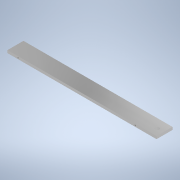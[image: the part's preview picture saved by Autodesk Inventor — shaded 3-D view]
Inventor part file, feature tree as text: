
AUTODESK INVENTOR PART (.ipt)
format: ipt  version: 2022 (Build 260153000, 153)  size: 131,584 bytes
history: native  units: mm
features: sketch x3, hole x2, other x1, extrude x1
ambient origin geometry x8: Origin, YZ Plane, XZ Plane, XY Plane, X Axis, Y Axis, Z Axis, Center Point
bodies: Body1 (feature_tree)
feature tree (7):
  other  "ソリッド1"
  extrude  "押し出し1"  Depth=30.0mm
  hole  "穴3"  [1 undecoded]
  hole  "穴5"  [1 undecoded]
  sketch  "スケッチ1"
  sketch  "スケッチ4"
  sketch  "スケッチ6"
note: 2 required parameter values undecoded (feature->parameter linkage not recoverable at this tier; creation-order binding heuristic only, values carry confidence <= 0.55)
